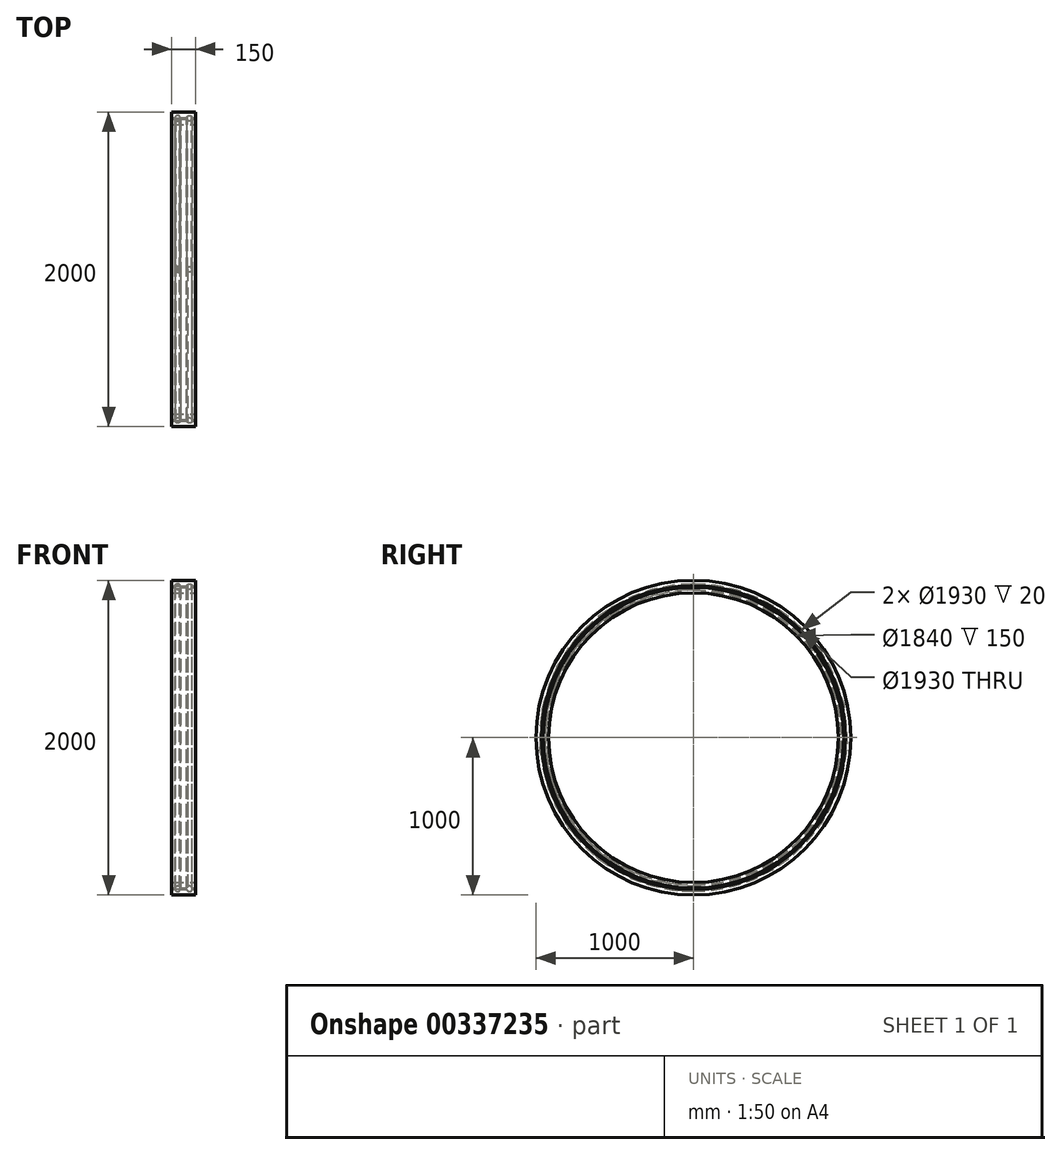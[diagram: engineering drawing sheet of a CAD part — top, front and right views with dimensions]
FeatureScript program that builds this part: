
annotation { "Feature Type Name" : "Feature", "Feature Type Description" : "" }
export const myFeature = defineFeature(function(context is Context, id is Id, definition is map)
    precondition{}
    {
        {
            var Q0;
            Q0=qCreatedBy(makeId("Front.planeOp"),FACE);
            var sketch = newSketch(context, id + "F0", { "sketchPlane" : qUnion([Q0])});
            skLineSegment(sketch, "E0.bottom", {"start": v(-75, 1000) * mm, "end": v(0, 1000) * mm});
            skLineSegment(sketch, "E0.top", {"start": v(-75, 965) * mm, "end": v(-55, 965) * mm});
            skLineSegment(sketch, "E0.left", {"start": v(-75, 1000) * mm, "end": v(-75, 965) * mm});
            skLineSegment(sketch, "E1", {"start": v(0, 1000) * mm, "end": v(0, 0) * mm, "construction": true});
            skCircle(sketch, "E2", {"center": v(-37.5, 960) * mm, "radius": 17.5 * mm});
            skArc(sketch, "E3", {"start": v(-20, 965) * mm, "mid": v(-37.5, 976.87) * mm, "end": v(-55, 965) * mm});
            skLineSegment(sketch, "E4.bottom", {"start": v(-75, 955) * mm, "end": v(-55, 955) * mm});
            skLineSegment(sketch, "E4.top", {"start": v(-75, 920) * mm, "end": v(0, 920) * mm});
            skLineSegment(sketch, "E4.left", {"start": v(-75, 955) * mm, "end": v(-75, 920) * mm});
            skArc(sketch, "E5", {"start": v(-55, 955) * mm, "mid": v(-37.5, 943.13) * mm, "end": v(-20, 955) * mm});
            skLineSegment(sketch, "E6", {"start": v(-37.5, 965) * mm, "end": v(-37.5, 955) * mm, "construction": true});
            skLineSegment(sketch, "E7.trimOffspring", {"start": v(-20, 965) * mm, "end": v(0, 965) * mm});
            skLineSegment(sketch, "E8.trimOffspring", {"start": v(-20, 955) * mm, "end": v(0, 955) * mm});
            skPoint(sketch, "E9.orphan", {"position": v(0, 965) * mm});
            skLineSegment(sketch, "E10.MirrorCS", {"start": v(37.5, 965) * mm, "end": v(37.5, 955) * mm, "construction": true});
            skLineSegment(sketch, "E11.MirrorCS", {"start": v(20, 955) * mm, "end": v(0, 955) * mm});
            skCircle(sketch, "E12.MirrorC", {"center": v(37.5, 960) * mm, "radius": 17.5 * mm});
            skLineSegment(sketch, "E13.MirrorCS", {"start": v(75, 965) * mm, "end": v(55, 965) * mm});
            skArc(sketch, "E14.MirrorCS", {"start": v(20, 965) * mm, "mid": v(37.5, 976.87) * mm, "end": v(55, 965) * mm});
            skLineSegment(sketch, "E15.MirrorCS", {"start": v(75, 1000) * mm, "end": v(0, 1000) * mm});
            skLineSegment(sketch, "E16.MirrorCS", {"start": v(75, 1000) * mm, "end": v(75, 965) * mm});
            skLineSegment(sketch, "E17.MirrorCS", {"start": v(75, 955) * mm, "end": v(55, 955) * mm});
            skLineSegment(sketch, "E18.MirrorCS", {"start": v(75, 920) * mm, "end": v(0, 920) * mm});
            skLineSegment(sketch, "E19.MirrorCS", {"start": v(75, 955) * mm, "end": v(75, 920) * mm});
            skArc(sketch, "E20.MirrorCS", {"start": v(55, 955) * mm, "mid": v(37.5, 943.13) * mm, "end": v(20, 955) * mm});
            skLineSegment(sketch, "E21.MirrorCS", {"start": v(20, 965) * mm, "end": v(0, 965) * mm});
            skLineSegment(sketch, "E22.bottom", {"start": v(-75, 920) * mm, "end": v(75, 920) * mm});
            skLineSegment(sketch, "E22.top", {"start": v(-75, 885) * mm, "end": v(75, 885) * mm});
            skLineSegment(sketch, "E22.left", {"start": v(-75, 920) * mm, "end": v(-75, 885) * mm});
            skLineSegment(sketch, "E22.right", {"start": v(75, 920) * mm, "end": v(75, 885) * mm});
            skLineSegment(sketch, "E23", {"start": v(0, 0) * mm, "end": v(-61.77, 0) * mm, "construction": true});
            skLineSegment(sketch, "E24", {"start": v(-55, 960) * mm, "end": v(-20, 960) * mm});
            skLineSegment(sketch, "E25.trimOffspring", {"start": v(20, 960) * mm, "end": v(55, 960) * mm});
            skLineSegment(sketch, "E26", {"start": v(0, 965) * mm, "end": v(0, 955) * mm, "construction": true});
            skLineSegment(sketch, "E27", {"start": v(0, 960) * mm, "end": v(-37.5, 960) * mm, "construction": true});
            skSolve(sketch);
        }
        {
            var Q0;
            {var subQ5=sQuery(id+"F0.wireOp",EDGE,"E4.bottom");Q0=makeQuery(id+"F0.imprint","IMPRINT",FACE,{"disambiguationData":[TD([[makeQuery(id+"F0.imprint","IMPRINT",EDGE,{"derivedFrom":subQ5}),-1.0]])]});}
            var Q1;
            Q1=makeQuery(id+"F0.imprint","IMPRINT",FACE,{"disambiguationData":[TD([[makeQuery(id+"F0.imprint","IMPRINT",EDGE,{"derivedFrom":sQuery(id+"F0.wireOp",EDGE,"E22.bottom")}),-1.0]])]});
            var Q2;
            {var subQ0=sQuery(id+"F0.wireOp",EDGE,"E20.MirrorCS");var subQ1=sQuery(id+"F0.wireOp",EDGE,"E12.MirrorC");var subQ2=makeQuery(id+"F0.imprint","INTERSECT",VERTEX,{"disambiguationData":[OD(0.0)],"derivedFrom":[subQ1,subQ0]});Q2=makeQuery(id+"F0.imprint","IMPRINT",FACE,{"disambiguationData":[TD([[makeQuery(id+"F0.imprint","IMPRINT",EDGE,{"disambiguationData":[TD([[subQ2,-1.0]])],"derivedFrom":subQ1}),-1.0]])]});}
            var Q3;
            {var subQ0=sQuery(id+"F0.wireOp",EDGE,"E5");var subQ1=sQuery(id+"F0.wireOp",EDGE,"E2");var subQ2=makeQuery(id+"F0.imprint","INTERSECT",VERTEX,{"disambiguationData":[OD(0.0)],"derivedFrom":[subQ1,subQ0]});Q3=makeQuery(id+"F0.imprint","IMPRINT",FACE,{"disambiguationData":[TD([[makeQuery(id+"F0.imprint","IMPRINT",EDGE,{"disambiguationData":[TD([[subQ2,-1.0]])],"derivedFrom":subQ1}),1.0]])]});}
            var Q4;
            Q4=sQuery(id+"F0.wireOp",EDGE,"E23");
            revolve(context, id + "F1", {"entities" : qUnion([Q0, Q1, Q2, Q3]), "axis" : qUnion([Q4]), "revolveType" : RevolveType.FULL});
        }
        {
            var Q0;
            {var subQ0=sQuery(id+"F0.wireOp",EDGE,"E24");Q0=makeQuery(id+"F0.imprint","IMPRINT",FACE,{"disambiguationData":[TD([[makeQuery(id+"F0.imprint","IMPRINT",EDGE,{"derivedFrom":subQ0}),1.0]])]});}
            var Q1;
            {var subQ0=sQuery(id+"F0.wireOp",EDGE,"E25.trimOffspring");Q1=makeQuery(id+"F0.imprint","IMPRINT",FACE,{"disambiguationData":[TD([[makeQuery(id+"F0.imprint","IMPRINT",EDGE,{"derivedFrom":subQ0}),1.0]])]});}
            var Q2;
            {var subQ0=sQuery(id+"F0.wireOp",EDGE,"E14.MirrorCS");var subQ1=sQuery(id+"F0.wireOp",EDGE,"E12.MirrorC");var subQ2=makeQuery(id+"F0.imprint","INTERSECT",VERTEX,{"disambiguationData":[OD(0.0)],"derivedFrom":[subQ1,subQ0]});Q2=makeQuery(id+"F0.imprint","IMPRINT",FACE,{"disambiguationData":[TD([[makeQuery(id+"F0.imprint","IMPRINT",EDGE,{"disambiguationData":[TD([[subQ2,1.0]])],"derivedFrom":subQ1}),-1.0]])]});}
            var Q3;
            {var subQ0=sQuery(id+"F0.wireOp",EDGE,"E3");var subQ1=sQuery(id+"F0.wireOp",EDGE,"E2");var subQ2=makeQuery(id+"F0.imprint","INTERSECT",VERTEX,{"disambiguationData":[OD(0.0)],"derivedFrom":[subQ1,subQ0]});Q3=makeQuery(id+"F0.imprint","IMPRINT",FACE,{"disambiguationData":[TD([[makeQuery(id+"F0.imprint","IMPRINT",EDGE,{"disambiguationData":[TD([[subQ2,1.0]])],"derivedFrom":subQ1}),1.0]])]});}
            var Q4;
            Q4=sQuery(id+"F0.wireOp",EDGE,"E24");
            revolve(context, id + "F2", {"operationType" : NewBodyOperationType.ADD, "entities" : qUnion([Q0, Q1, Q2, Q3]), "axis" : qUnion([Q4]), "revolveType" : RevolveType.FULL});
        }
        {
            var Q0;
            Q0=makeQuery(id+"F0.imprint","IMPRINT",FACE,{"disambiguationData":[TD([[makeQuery(id+"F0.imprint","IMPRINT",EDGE,{"derivedFrom":sQuery(id+"F0.wireOp",EDGE,"E0.bottom")}),-1.0]])]});
            var Q1;
            {var subQ0=sQuery(id+"F0.wireOp",EDGE,"E14.MirrorCS");var subQ1=sQuery(id+"F0.wireOp",EDGE,"E12.MirrorC");var subQ2=makeQuery(id+"F0.imprint","INTERSECT",VERTEX,{"disambiguationData":[OD(0.0)],"derivedFrom":[subQ1,subQ0]});Q1=makeQuery(id+"F0.imprint","IMPRINT",FACE,{"disambiguationData":[TD([[makeQuery(id+"F0.imprint","IMPRINT",EDGE,{"disambiguationData":[TD([[subQ2,1.0]])],"derivedFrom":subQ1}),-1.0]])]});}
            var Q2;
            {var subQ0=sQuery(id+"F0.wireOp",EDGE,"E3");var subQ1=sQuery(id+"F0.wireOp",EDGE,"E2");var subQ2=makeQuery(id+"F0.imprint","INTERSECT",VERTEX,{"disambiguationData":[OD(0.0)],"derivedFrom":[subQ1,subQ0]});Q2=makeQuery(id+"F0.imprint","IMPRINT",FACE,{"disambiguationData":[TD([[makeQuery(id+"F0.imprint","IMPRINT",EDGE,{"disambiguationData":[TD([[subQ2,1.0]])],"derivedFrom":subQ1}),1.0]])]});}
            var Q3;
            Q3=sQuery(id+"F0.wireOp",EDGE,"E23");
            revolve(context, id + "F3", {"operationType" : NewBodyOperationType.ADD, "entities" : qUnion([Q0, Q1, Q2]), "axis" : qUnion([Q3]), "revolveType" : RevolveType.FULL});
        }
        {
            var Q0;
            Q0=makeQuery(id+"F1.opRevolve","SWEPT_FACE",FACE,{"disambiguationData":[OSD([sQuery(id+"F0.wireOp",EDGE,"E19.MirrorCS"),sQuery(id+"F0.wireOp",EDGE,"E22.right")])]});
            var sketch = newSketch(context, id + "F4", { "sketchPlane" : qUnion([Q0])});
            skCircle(sketch, "E28", {"center": v(0, 0) * mm, "radius": 925 * mm});
            skCircle(sketch, "E29.0", {"center": v(0, 0) * mm, "radius": 885 * mm});
            skArc(sketch, "E30", {"start": v(-15, 884.87) * mm, "mid": v(-9.73, 902.9) * mm, "end": v(-5, 921.07) * mm});
            skArc(sketch, "E31", {"start": v(0, 925) * mm, "mid": v(-3.18, 923.9) * mm, "end": v(-5, 921.07) * mm});
            skArc(sketch, "E32.MirrorCS", {"start": v(15, 884.87) * mm, "mid": v(9.73, 902.9) * mm, "end": v(5, 921.07) * mm});
            skArc(sketch, "E33.MirrorCS", {"start": v(0, 925) * mm, "mid": v(3.18, 923.9) * mm, "end": v(5, 921.07) * mm});
            skLineSegment(sketch, "E34", {"start": v(-9.66, 925) * mm, "end": v(9.66, 925) * mm});
            skSolve(sketch);
        }
        {
            var Q0;
            {var subQ1=sQuery(id+"F4.wireOp",EDGE,"E30");Q0=makeQuery(id+"F4.imprint","IMPRINT",FACE,{"disambiguationData":[TD([[makeQuery(id+"F4.imprint","IMPRINT",EDGE,{"derivedFrom":subQ1}),-1.0]])]});}
            extrude(context, id + "F5", {"entities" : qUnion([Q0]), "operationType" : NewBodyOperationType.REMOVE, "endBound" : BoundingType.THROUGH_ALL, "oppositeDirection" : true, "depth" : 25 * mm});
        }
    });
